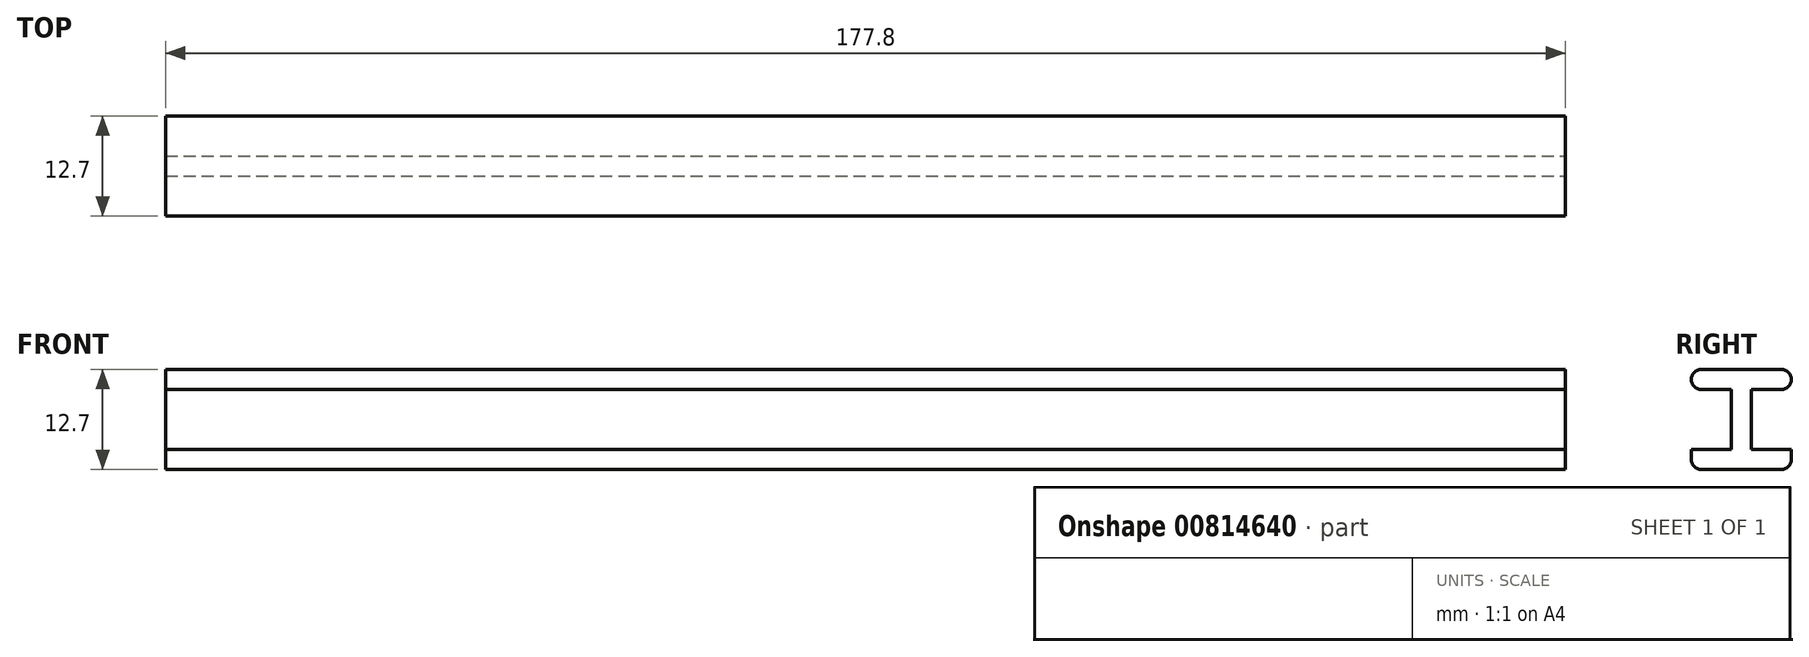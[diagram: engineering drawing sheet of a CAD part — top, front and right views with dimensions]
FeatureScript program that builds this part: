
annotation { "Feature Type Name" : "Feature", "Feature Type Description" : "" }
export const myFeature = defineFeature(function(context is Context, id is Id, definition is map)
    precondition{}
    {
        {
            var Q0;
            Q0=qCreatedBy(makeId("Top.planeOp"),FACE);
            var sketch = newSketch(context, id + "F0", { "sketchPlane" : qUnion([Q0])});
            skLineSegment(sketch, "E0.bottom", {"start": v(88.9, -6.35) * mm, "end": v(-88.9, -6.35) * mm});
            skLineSegment(sketch, "E0.top", {"start": v(88.9, 6.35) * mm, "end": v(-88.9, 6.35) * mm});
            skLineSegment(sketch, "E0.left", {"start": v(88.9, -6.35) * mm, "end": v(88.9, 6.35) * mm});
            skLineSegment(sketch, "E0.right", {"start": v(-88.9, -6.35) * mm, "end": v(-88.9, 6.35) * mm});
            skPoint(sketch, "E0.middle", {"position": v(0, 0) * mm});
            skSolve(sketch);
        }
        {
            var Q0;
            Q0=makeQuery(id+"F0.imprint","IMPRINT",FACE,{"disambiguationData":[TD([[makeQuery(id+"F0.imprint","IMPRINT",EDGE,{"derivedFrom":sQuery(id+"F0.wireOp",EDGE,"E0.bottom")}),-1.0]])]});
            extrude(context, id + "F1", {"entities" : qUnion([Q0]), "depth" : 12.7 * mm, "offsetDistance" : 25.4 * mm});
        }
        {
            var Q0;
            Q0=makeQuery(id+"F1.opExtrude","CAP_EDGE",EDGE,{"disambiguationData":[OSD([sQuery(id+"F0.wireOp",EDGE,"E0.top")])],"isStart":true});
            var Q1;
            Q1=makeQuery(id+"F1.opExtrude","CAP_EDGE",EDGE,{"disambiguationData":[OSD([sQuery(id+"F0.wireOp",EDGE,"E0.top")])],"isStart":false});
            var Q2;
            Q2=makeQuery(id+"F1.opExtrude","CAP_EDGE",EDGE,{"disambiguationData":[OSD([sQuery(id+"F0.wireOp",EDGE,"E0.bottom")])],"isStart":false});
            var Q3;
            Q3=makeQuery(id+"F1.opExtrude","CAP_EDGE",EDGE,{"disambiguationData":[OSD([sQuery(id+"F0.wireOp",EDGE,"E0.bottom")])],"isStart":true});
            fillet(context, id + "F2", {"entities" : qUnion([Q0, Q1, Q2, Q3]), "radius" : 1.27 * mm, "tangentPropagation" : true, "defaultsChanged" : false, "vertexSettings" : [], "allowEdgeOverflow" : false});
        }
        {
            var Q0;
            Q0=makeQuery(id+"F1.opExtrude","SWEPT_FACE",FACE,{"disambiguationData":[OSD([sQuery(id+"F0.wireOp",EDGE,"E0.left")])]});
            var sketch = newSketch(context, id + "F3", { "sketchPlane" : qUnion([Q0])});
            skLineSegment(sketch, "E1.bottom", {"start": v(-6.35, 10.16) * mm, "end": v(-1.27, 10.16) * mm});
            skLineSegment(sketch, "E1.top", {"start": v(-6.35, 2.54) * mm, "end": v(-1.27, 2.54) * mm});
            skLineSegment(sketch, "E1.left", {"start": v(-6.35, 10.16) * mm, "end": v(-6.35, 2.54) * mm});
            skLineSegment(sketch, "E1.right", {"start": v(-1.27, 10.16) * mm, "end": v(-1.27, 2.54) * mm});
            skLineSegment(sketch, "E2.bottom", {"start": v(6.35, 10.16) * mm, "end": v(1.27, 10.16) * mm});
            skLineSegment(sketch, "E2.top", {"start": v(6.35, 2.54) * mm, "end": v(1.27, 2.54) * mm});
            skLineSegment(sketch, "E2.left", {"start": v(6.35, 10.16) * mm, "end": v(6.35, 2.54) * mm});
            skLineSegment(sketch, "E2.right", {"start": v(1.27, 10.16) * mm, "end": v(1.27, 2.54) * mm});
            skSolve(sketch);
        }
        {
            var Q0;
            Q0=makeQuery(id+"F3.imprint","IMPRINT",FACE,{"disambiguationData":[TD([[makeQuery(id+"F3.imprint","IMPRINT",EDGE,{"derivedFrom":sQuery(id+"F3.wireOp",EDGE,"E1.bottom")}),-1.0]])]});
            var Q1;
            Q1=makeQuery(id+"F3.imprint","IMPRINT",FACE,{"disambiguationData":[TD([[makeQuery(id+"F3.imprint","IMPRINT",EDGE,{"derivedFrom":sQuery(id+"F3.wireOp",EDGE,"E2.bottom")}),1.0]])]});
            extrude(context, id + "F4", {"entities" : qUnion([Q0, Q1]), "operationType" : NewBodyOperationType.REMOVE, "oppositeDirection" : true, "depth" : 177.8 * mm, "offsetDistance" : 25.4 * mm});
        }
        {
            var Q0;
            Q0=makeQuery(id+"F4.boolean.opBoolean","COPY",EDGE,{"derivedFrom":makeQuery(id+"F4.opExtrude","SWEPT_EDGE",EDGE,{"disambiguationData":[OSD([sQuery(id+"F0.wireOp",EDGE,"E0.top"),sQuery(id+"F0.wireOp",EDGE,"E0.left"),sQuery(id+"F3.wireOp",EDGE,"E2.bottom"),sQuery(id+"F3.wireOp",EDGE,"E2.left")])]})});
            var Q1;
            Q1=makeQuery(id+"F4.boolean.opBoolean","COPY",EDGE,{"derivedFrom":makeQuery(id+"F4.opExtrude","SWEPT_EDGE",EDGE,{"disambiguationData":[OSD([sQuery(id+"F0.wireOp",EDGE,"E0.top"),sQuery(id+"F0.wireOp",EDGE,"E0.left"),sQuery(id+"F3.wireOp",EDGE,"E2.top"),sQuery(id+"F3.wireOp",EDGE,"E2.left")])]})});
            var Q2;
            Q2=makeQuery(id+"F4.boolean.opBoolean","COPY",EDGE,{"derivedFrom":makeQuery(id+"F4.opExtrude","SWEPT_EDGE",EDGE,{"disambiguationData":[OSD([sQuery(id+"F0.wireOp",EDGE,"E0.bottom"),sQuery(id+"F0.wireOp",EDGE,"E0.left"),sQuery(id+"F3.wireOp",EDGE,"E1.bottom"),sQuery(id+"F3.wireOp",EDGE,"E1.left")])]})});
            var Q3;
            Q3=makeQuery(id+"F4.boolean.opBoolean","COPY",EDGE,{"derivedFrom":makeQuery(id+"F4.opExtrude","SWEPT_EDGE",EDGE,{"disambiguationData":[OSD([sQuery(id+"F0.wireOp",EDGE,"E0.bottom"),sQuery(id+"F0.wireOp",EDGE,"E0.left"),sQuery(id+"F3.wireOp",EDGE,"E1.top"),sQuery(id+"F3.wireOp",EDGE,"E1.left")])]})});
            fillet(context, id + "F5", {"entities" : qUnion([Q0, Q1, Q2, Q3]), "radius" : 1.27 * mm, "tangentPropagation" : true, "defaultsChanged" : false, "vertexSettings" : [], "allowEdgeOverflow" : false});
        }
    });
